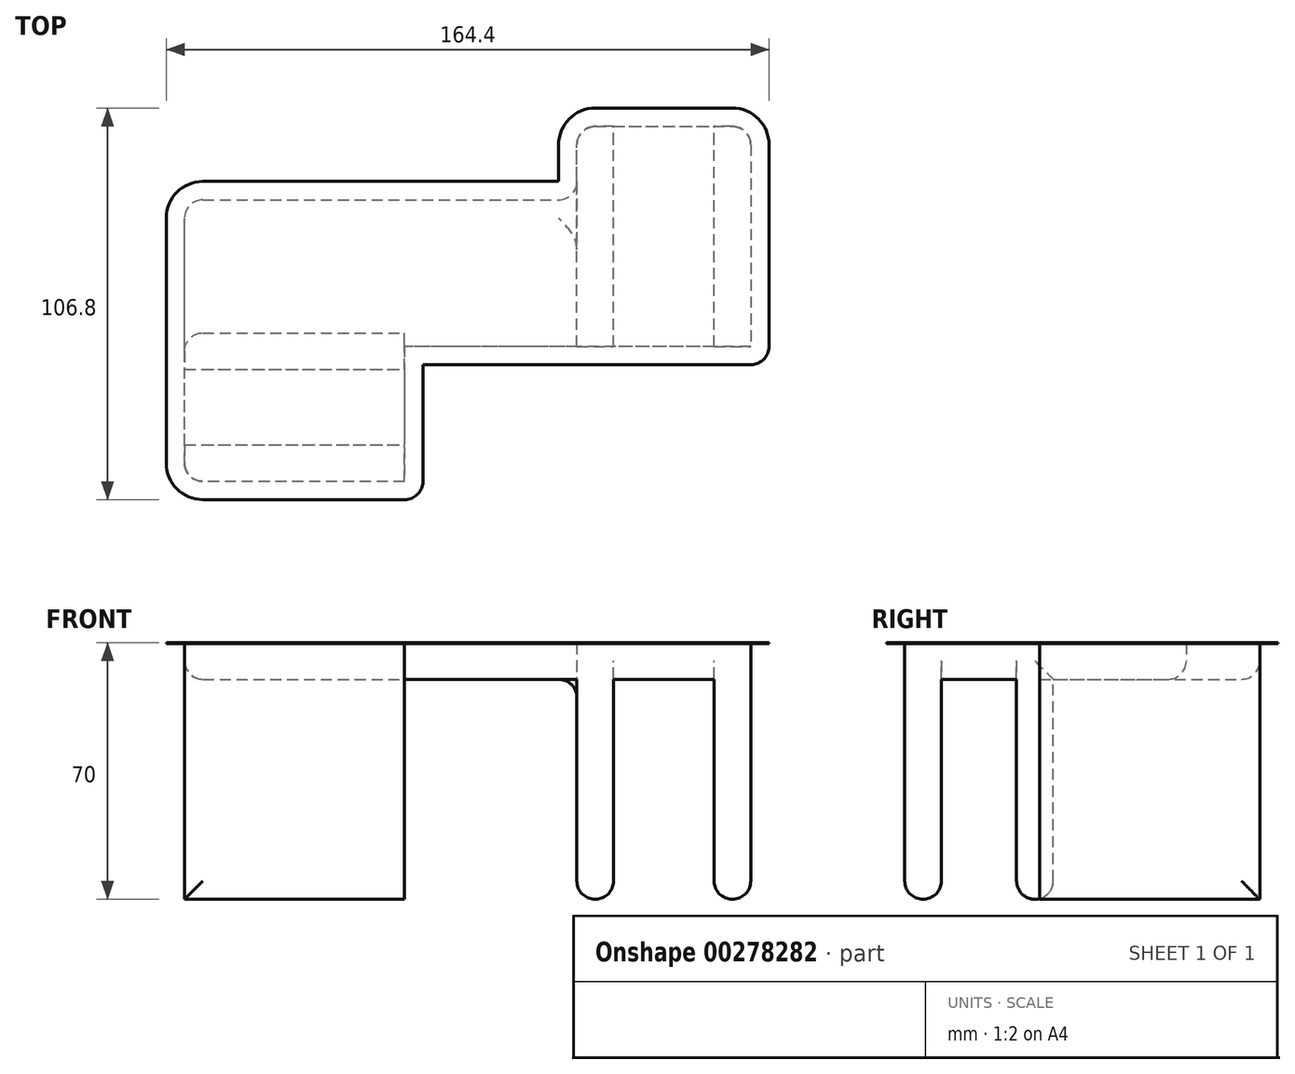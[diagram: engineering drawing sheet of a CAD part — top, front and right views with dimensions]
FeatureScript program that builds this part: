
annotation { "Feature Type Name" : "Feature", "Feature Type Description" : "" }
export const myFeature = defineFeature(function(context is Context, id is Id, definition is map)
    precondition{}
    {
        {
            var Q0;
            Q0=qCreatedBy(makeId("Top.planeOp"),FACE);
            var sketch = newSketch(context, id + "F0", { "sketchPlane" : qUnion([Q0])});
            skLineSegment(sketch, "E0", {"start": v(0, 0) * mm, "end": v(50, 0) * mm, "construction": true});
            skLineSegment(sketch, "E1", {"start": v(0, 18.5) * mm, "end": v(50, 18.5) * mm, "construction": true});
            skLineSegment(sketch, "E2.bottom", {"start": v(50, 24.8) * mm, "end": v(138.7, 24.8) * mm, "construction": true});
            skLineSegment(sketch, "E2.top", {"start": v(50, -6.3) * mm, "end": v(138.7, -6.3) * mm, "construction": true});
            skLineSegment(sketch, "E2.left", {"start": v(50, 24.8) * mm, "end": v(50, -6.3) * mm, "construction": true});
            skLineSegment(sketch, "E2.right", {"start": v(138.7, 24.8) * mm, "end": v(138.7, -6.3) * mm, "construction": true});
            skLineSegment(sketch, "E3", {"start": v(107, 24.8) * mm, "end": v(107, 74.8) * mm, "construction": true});
            skLineSegment(sketch, "E4", {"start": v(132.4, 24.8) * mm, "end": v(132.4, 74.8) * mm, "construction": true});
            skLineSegment(sketch, "E5", {"start": v(132.4, 74.8) * mm, "end": v(107, 74.8) * mm, "construction": true});
            skLineSegment(sketch, "E6", {"start": v(0, 18.5) * mm, "end": v(0, 0) * mm, "construction": true});
            skSolve(sketch);
        }
        {
            var Q0;
            Q0=qCreatedBy(makeId("Top.planeOp"),FACE);
            var sketch = newSketch(context, id + "F1", { "sketchPlane" : qUnion([Q0])});
            skLineSegment(sketch, "E7", {"start": v(-11, -11) * mm, "end": v(-11, 65.8) * mm});
            skLineSegment(sketch, "E8", {"start": v(96, 85.8) * mm, "end": v(143.4, 85.8) * mm});
            skLineSegment(sketch, "E9", {"start": v(143.4, 85.8) * mm, "end": v(143.4, 25.8) * mm});
            skLineSegment(sketch, "E10", {"start": v(143.4, 25.8) * mm, "end": v(49, 25.8) * mm});
            skLineSegment(sketch, "E11", {"start": v(49, 25.8) * mm, "end": v(49, -11) * mm});
            skLineSegment(sketch, "E12", {"start": v(49, -11) * mm, "end": v(-11, -11) * mm});
            skLineSegment(sketch, "E13", {"start": v(-11, -1) * mm, "end": v(49, -1) * mm, "construction": true});
            skLineSegment(sketch, "E14", {"start": v(-11, 19.5) * mm, "end": v(49, 19.5) * mm, "construction": true});
            skLineSegment(sketch, "E15", {"start": v(106, 85.8) * mm, "end": v(106, 25.8) * mm, "construction": true});
            skLineSegment(sketch, "E16", {"start": v(133.4, 85.8) * mm, "end": v(133.4, 25.8) * mm, "construction": true});
            skLineSegment(sketch, "E17", {"start": v(-11, 65.8) * mm, "end": v(96, 65.8) * mm});
            skLineSegment(sketch, "E18", {"start": v(96, 65.8) * mm, "end": v(96, 85.8) * mm});
            skSolve(sketch);
        }
        {
            var Q0;
            Q0=qSketchRegion(id+"F1",true);
            extrude(context, id + "F2", {"entities" : qUnion([Q0]), "depth" : 10 * mm, "offsetDistance" : 25 * mm});
        }
        {
            var Q0;
            Q0=makeQuery(id+"F2.opExtrude","CAP_FACE",FACE,{"disambiguationData":[OSD([sQuery(id+"F1.wireOp",EDGE,"E7"),sQuery(id+"F1.wireOp",EDGE,"E8"),sQuery(id+"F1.wireOp",EDGE,"E9"),sQuery(id+"F1.wireOp",EDGE,"E10"),sQuery(id+"F1.wireOp",EDGE,"E11"),sQuery(id+"F1.wireOp",EDGE,"E12")])],"isStart":true});
            var sketch = newSketch(context, id + "F3", { "sketchPlane" : qUnion([Q0])});
            skLineSegment(sketch, "E19.bottom", {"start": v(-11, 11) * mm, "end": v(49, 11) * mm});
            skLineSegment(sketch, "E19.top", {"start": v(-11, 1) * mm, "end": v(49, 1) * mm});
            skLineSegment(sketch, "E19.left", {"start": v(-11, 11) * mm, "end": v(-11, 1) * mm});
            skLineSegment(sketch, "E19.right", {"start": v(49, 11) * mm, "end": v(49, 1) * mm});
            skLineSegment(sketch, "E20.bottom", {"start": v(-11, -19.5) * mm, "end": v(49, -19.5) * mm});
            skLineSegment(sketch, "E20.top", {"start": v(-11, -29.5) * mm, "end": v(49, -29.5) * mm});
            skLineSegment(sketch, "E20.left", {"start": v(-11, -19.5) * mm, "end": v(-11, -29.5) * mm});
            skLineSegment(sketch, "E20.right", {"start": v(49, -19.5) * mm, "end": v(49, -29.5) * mm});
            skLineSegment(sketch, "E21.bottom", {"start": v(96, -25.8) * mm, "end": v(106, -25.8) * mm});
            skLineSegment(sketch, "E21.top", {"start": v(96, -85.8) * mm, "end": v(106, -85.8) * mm});
            skLineSegment(sketch, "E21.left", {"start": v(96, -25.8) * mm, "end": v(96, -85.8) * mm});
            skLineSegment(sketch, "E21.right", {"start": v(106, -25.8) * mm, "end": v(106, -85.8) * mm});
            skLineSegment(sketch, "E22.bottom", {"start": v(143.4, -25.8) * mm, "end": v(133.4, -25.8) * mm});
            skLineSegment(sketch, "E22.top", {"start": v(143.4, -85.8) * mm, "end": v(133.4, -85.8) * mm});
            skLineSegment(sketch, "E22.left", {"start": v(143.4, -25.8) * mm, "end": v(143.4, -85.8) * mm});
            skLineSegment(sketch, "E22.right", {"start": v(133.4, -25.8) * mm, "end": v(133.4, -85.8) * mm});
            skSolve(sketch);
        }
        {
            var Q0;
            Q0=qSketchRegion(id+"F3",true);
            extrude(context, id + "F4", {"entities" : qUnion([Q0]), "operationType" : NewBodyOperationType.ADD, "depth" : 60 * mm, "offsetDistance" : 25 * mm});
        }
        {
            var Q0;
            Q0=makeQuery(id+"F2.opExtrude","SWEPT_EDGE",EDGE,{"disambiguationData":[OSD([sQuery(id+"F1.wireOp",EDGE,"E17"),sQuery(id+"F1.wireOp",EDGE,"E18")])]});
            var Q1;
            Q1=makeQuery(id+"F4.boolean.opBoolean","MERGE",EDGE,{"derivedFrom":[makeQuery(id+"F2.opExtrude","SWEPT_EDGE",EDGE,{"disambiguationData":[OSD([sQuery(id+"F1.wireOp",EDGE,"E8"),sQuery(id+"F1.wireOp",EDGE,"E18")])]}),makeQuery(id+"F4.opExtrude","SWEPT_EDGE",EDGE,{"disambiguationData":[OSD([sQuery(id+"F3.wireOp",EDGE,"E21.top"),sQuery(id+"F3.wireOp",EDGE,"E21.left")])]})]});
            var Q2;
            Q2=makeQuery(id+"F4.boolean.opBoolean","MERGE",EDGE,{"derivedFrom":[makeQuery(id+"F2.opExtrude","SWEPT_EDGE",EDGE,{"disambiguationData":[OSD([sQuery(id+"F1.wireOp",EDGE,"E8"),sQuery(id+"F1.wireOp",EDGE,"E9")])]}),makeQuery(id+"F4.opExtrude","SWEPT_EDGE",EDGE,{"disambiguationData":[OSD([sQuery(id+"F3.wireOp",EDGE,"E22.top"),sQuery(id+"F3.wireOp",EDGE,"E22.left")])]})]});
            var Q3;
            Q3=makeQuery(id+"F2.opExtrude","SWEPT_EDGE",EDGE,{"disambiguationData":[OSD([sQuery(id+"F1.wireOp",EDGE,"E7"),sQuery(id+"F1.wireOp",EDGE,"E17")])]});
            var Q4;
            Q4=makeQuery(id+"F4.opExtrude","SWEPT_EDGE",EDGE,{"disambiguationData":[OSD([sQuery(id+"F1.wireOp",EDGE,"E7"),sQuery(id+"F3.wireOp",EDGE,"E20.top"),sQuery(id+"F3.wireOp",EDGE,"E20.left")])]});
            var Q5;
            Q5=makeQuery(id+"F4.boolean.opBoolean","MERGE",EDGE,{"derivedFrom":[makeQuery(id+"F2.opExtrude","SWEPT_EDGE",EDGE,{"disambiguationData":[OSD([sQuery(id+"F1.wireOp",EDGE,"E7"),sQuery(id+"F1.wireOp",EDGE,"E12")])]}),makeQuery(id+"F4.opExtrude","SWEPT_EDGE",EDGE,{"disambiguationData":[OSD([sQuery(id+"F3.wireOp",EDGE,"E19.bottom"),sQuery(id+"F3.wireOp",EDGE,"E19.left")])]})]});
            var Q6;
            Q6=makeQuery(id+"F2.opExtrude","CAP_EDGE",EDGE,{"disambiguationData":[OSD([sQuery(id+"F1.wireOp",EDGE,"E8")])],"isStart":true});
            var Q7;
            Q7=makeQuery(id+"F2.opExtrude","CAP_EDGE",EDGE,{"disambiguationData":[OSD([sQuery(id+"F1.wireOp",EDGE,"E17")])],"isStart":true});
            var Q8;
            {var subQ0=sQuery(id+"F1.wireOp",EDGE,"E17");var subQ1=sQuery(id+"F1.wireOp",EDGE,"E7");Q8=makeQuery(id+"F4.boolean.opBoolean","SPLIT",EDGE,{"disambiguationData":[TD([makeQuery(id+"F2.opExtrude","SWEPT_FACE",FACE,{"disambiguationData":[OSD([subQ0])]})])],"derivedFrom":makeQuery(id+"F2.opExtrude","CAP_EDGE",EDGE,{"disambiguationData":[OSD([subQ1])],"isStart":true})});}
            var Q9;
            {var subQ0=sQuery(id+"F1.wireOp",EDGE,"E7");Q9=makeQuery(id+"F4.boolean.opBoolean","SPLIT",EDGE,{"disambiguationData":[TD([makeQuery(id+"F4.opExtrude","SWEPT_FACE",FACE,{"disambiguationData":[OSD([sQuery(id+"F3.wireOp",EDGE,"E19.top")])]})])],"derivedFrom":makeQuery(id+"F2.opExtrude","CAP_EDGE",EDGE,{"disambiguationData":[OSD([subQ0])],"isStart":true})});}
            var Q10;
            Q10=makeQuery(id+"F4.opExtrude","CAP_EDGE",EDGE,{"disambiguationData":[OSD([sQuery(id+"F3.wireOp",EDGE,"E22.right")])],"isStart":false});
            var Q11;
            Q11=makeQuery(id+"F4.opExtrude","CAP_EDGE",EDGE,{"disambiguationData":[OSD([sQuery(id+"F3.wireOp",EDGE,"E21.right")])],"isStart":false});
            var Q12;
            Q12=makeQuery(id+"F4.opExtrude","CAP_EDGE",EDGE,{"disambiguationData":[OSD([sQuery(id+"F3.wireOp",EDGE,"E21.left")])],"isStart":false});
            var Q13;
            Q13=makeQuery(id+"F4.opExtrude","CAP_EDGE",EDGE,{"disambiguationData":[OSD([sQuery(id+"F3.wireOp",EDGE,"E22.left")])],"isStart":false});
            var Q14;
            Q14=makeQuery(id+"F4.opExtrude","CAP_EDGE",EDGE,{"disambiguationData":[OSD([sQuery(id+"F3.wireOp",EDGE,"E20.top")])],"isStart":true});
            var Q15;
            Q15=makeQuery(id+"F4.opExtrude","CAP_EDGE",EDGE,{"disambiguationData":[OSD([sQuery(id+"F3.wireOp",EDGE,"E20.top")])],"isStart":false});
            var Q16;
            Q16=makeQuery(id+"F4.opExtrude","CAP_EDGE",EDGE,{"disambiguationData":[OSD([sQuery(id+"F3.wireOp",EDGE,"E19.bottom")])],"isStart":false});
            var Q17;
            Q17=makeQuery(id+"F4.opExtrude","CAP_EDGE",EDGE,{"disambiguationData":[OSD([sQuery(id+"F3.wireOp",EDGE,"E19.top")])],"isStart":false});
            var Q18;
            Q18=makeQuery(id+"F4.opExtrude","CAP_EDGE",EDGE,{"disambiguationData":[OSD([sQuery(id+"F3.wireOp",EDGE,"E20.bottom")])],"isStart":false});
            fillet(context, id + "F5", {"entities" : qUnion([Q0, Q1, Q2, Q3, Q4, Q5, Q6, Q7, Q8, Q9, Q10, Q11, Q12, Q13, Q14, Q15, Q16, Q17, Q18]), "radius" : 5 * mm, "tangentPropagation" : true, "allowEdgeOverflow" : false});
        }
        {
            var Q0;
            Q0=makeQuery(id+"F2.opExtrude","CAP_FACE",FACE,{"disambiguationData":[OSD([sQuery(id+"F1.wireOp",EDGE,"E7"),sQuery(id+"F1.wireOp",EDGE,"E8"),sQuery(id+"F1.wireOp",EDGE,"E9"),sQuery(id+"F1.wireOp",EDGE,"E10"),sQuery(id+"F1.wireOp",EDGE,"E11"),sQuery(id+"F1.wireOp",EDGE,"E12"),sQuery(id+"F1.wireOp",EDGE,"E17"),sQuery(id+"F1.wireOp",EDGE,"E18")])],"isStart":false});
            var sketch = newSketch(context, id + "F6", { "sketchPlane" : qUnion([Q0])});
            skLineSegment(sketch, "E23", {"start": v(-11, 60.8) * mm, "end": v(-11, -6) * mm});
            skLineSegment(sketch, "E24", {"start": v(-6, 65.8) * mm, "end": v(91, 65.8) * mm});
            skLineSegment(sketch, "E25", {"start": v(-6, -11) * mm, "end": v(49, -11) * mm});
            skLineSegment(sketch, "E26", {"start": v(49, -11) * mm, "end": v(49, 25.8) * mm});
            skLineSegment(sketch, "E27", {"start": v(49, 25.8) * mm, "end": v(143.4, 25.8) * mm});
            skLineSegment(sketch, "E28", {"start": v(143.4, 25.8) * mm, "end": v(143.4, 80.8) * mm});
            skLineSegment(sketch, "E29", {"start": v(96, 70.8) * mm, "end": v(96, 80.8) * mm});
            skLineSegment(sketch, "E30", {"start": v(101, 85.8) * mm, "end": v(138.4, 85.8) * mm});
            skArc(sketch, "E31", {"start": v(-6, 65.8) * mm, "mid": v(-9.54, 64.34) * mm, "end": v(-11, 60.8) * mm});
            skArc(sketch, "E32", {"start": v(-11, -6) * mm, "mid": v(-9.54, -9.54) * mm, "end": v(-6, -11) * mm});
            skArc(sketch, "E33", {"start": v(91, 65.8) * mm, "mid": v(94.54, 67.26) * mm, "end": v(96, 70.8) * mm});
            skArc(sketch, "E34", {"start": v(101, 85.8) * mm, "mid": v(97.46, 84.34) * mm, "end": v(96, 80.8) * mm});
            skArc(sketch, "E35", {"start": v(143.4, 80.8) * mm, "mid": v(141.94, 84.34) * mm, "end": v(138.4, 85.8) * mm});
            skLineSegment(sketch, "E36", {"start": v(-16, 60.8) * mm, "end": v(-16, -6) * mm});
            skLineSegment(sketch, "E37", {"start": v(-6, 70.8) * mm, "end": v(91, 70.8) * mm});
            skLineSegment(sketch, "E38", {"start": v(101, 90.8) * mm, "end": v(138.4, 90.8) * mm});
            skLineSegment(sketch, "E39", {"start": v(148.4, 80.8) * mm, "end": v(148.4, 25.8) * mm});
            skLineSegment(sketch, "E40", {"start": v(54, 20.8) * mm, "end": v(143.4, 20.8) * mm});
            skLineSegment(sketch, "E41", {"start": v(54, 20.8) * mm, "end": v(54, -11) * mm});
            skLineSegment(sketch, "E42", {"start": v(-6, -16) * mm, "end": v(49, -16) * mm});
            skArc(sketch, "E43", {"start": v(-6, 70.8) * mm, "mid": v(-13.07, 67.87) * mm, "end": v(-16, 60.8) * mm});
            skArc(sketch, "E44", {"start": v(-16, -6) * mm, "mid": v(-13.07, -13.07) * mm, "end": v(-6, -16) * mm});
            skArc(sketch, "E45", {"start": v(49, -16) * mm, "mid": v(52.54, -14.54) * mm, "end": v(54, -11) * mm});
            skLineSegment(sketch, "E46", {"start": v(91, 70.8) * mm, "end": v(91, 80.8) * mm});
            skArc(sketch, "E47", {"start": v(101, 90.8) * mm, "mid": v(93.93, 87.87) * mm, "end": v(91, 80.8) * mm});
            skArc(sketch, "E48", {"start": v(148.4, 80.8) * mm, "mid": v(145.47, 87.87) * mm, "end": v(138.4, 90.8) * mm});
            skArc(sketch, "E49", {"start": v(143.4, 20.8) * mm, "mid": v(146.94, 22.26) * mm, "end": v(148.4, 25.8) * mm});
            skSolve(sketch);
        }
        {
            var Q0;
            Q0 = qSketchRegion(id + "F6", true);
            extrude(context, id + "F7", {"entities" : qUnion([Q0]), "operationType" : NewBodyOperationType.ADD, "oppositeDirection" : true, "depth" : 0.2 * mm, "offsetDistance" : 25 * mm});
        }
    });
